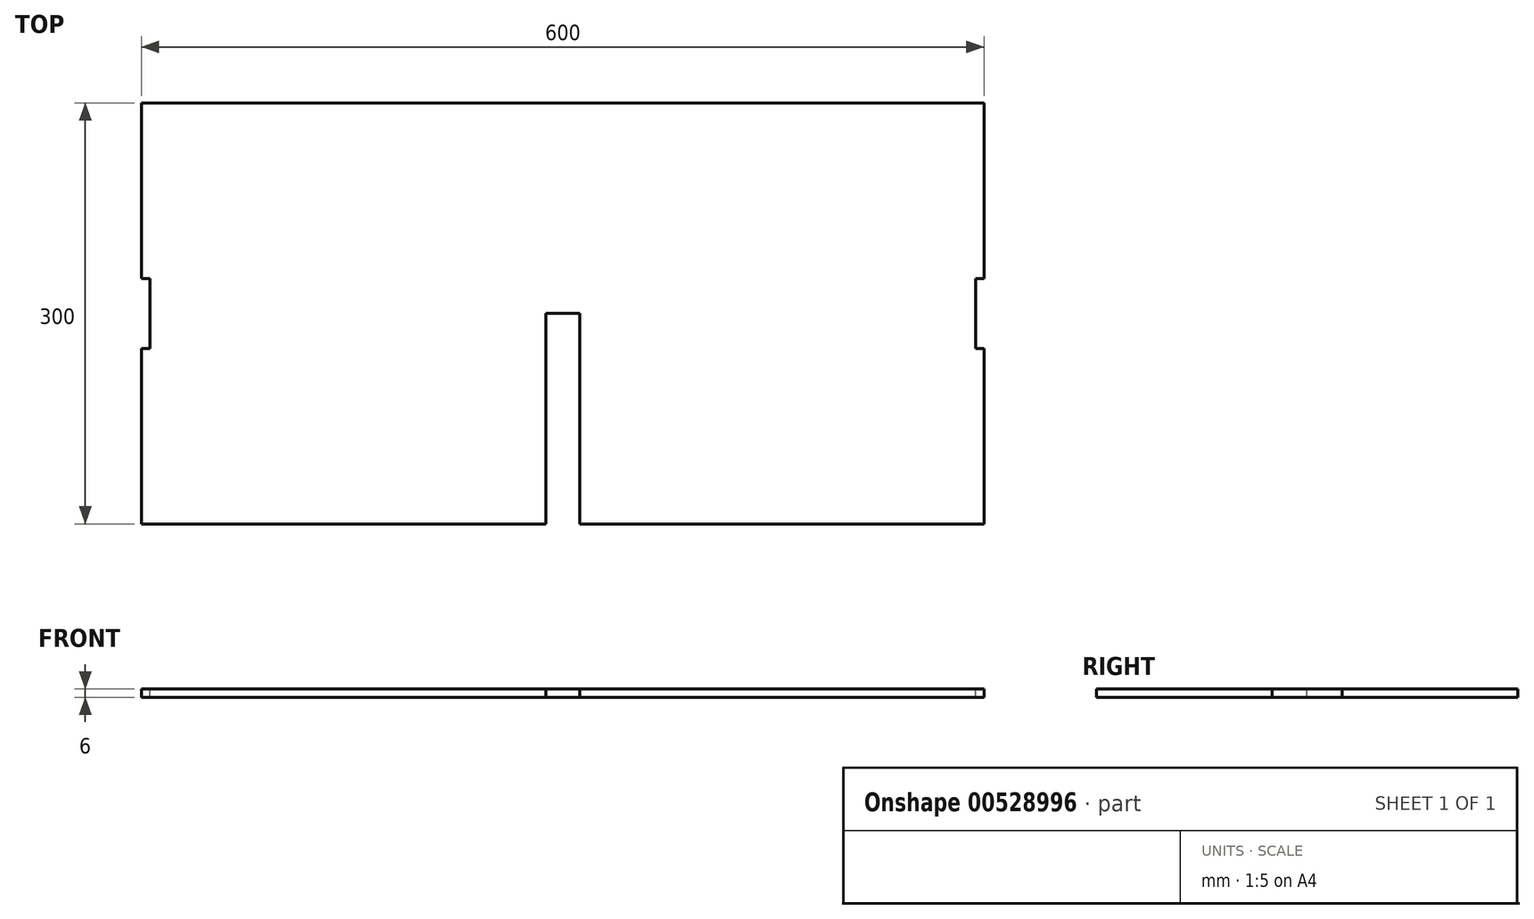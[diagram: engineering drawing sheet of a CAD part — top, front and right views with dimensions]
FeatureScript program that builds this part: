
annotation { "Feature Type Name" : "Feature", "Feature Type Description" : "" }
export const myFeature = defineFeature(function(context is Context, id is Id, definition is map)
    precondition{}
    {
        {
            var Q0;
            Q0=qCreatedBy(makeId("Front.planeOp"),FACE);
            var sketch = newSketch(context, id + "F0", { "sketchPlane" : qUnion([Q0])});
            skLineSegment(sketch, "E0.bottom", {"start": v(-213.98, 78.73) * mm, "end": v(386.02, 78.73) * mm});
            skLineSegment(sketch, "E0.top", {"start": v(-213.98, 72.73) * mm, "end": v(386.02, 72.73) * mm});
            skLineSegment(sketch, "E0.left", {"start": v(-213.98, 78.73) * mm, "end": v(-213.98, 72.73) * mm});
            skLineSegment(sketch, "E0.right", {"start": v(386.02, 78.73) * mm, "end": v(386.02, 72.73) * mm});
            skLineSegment(sketch, "E1", {"start": v(74.02, 78.73) * mm, "end": v(74.02, 72.73) * mm});
            skLineSegment(sketch, "E2", {"start": v(98.02, 78.73) * mm, "end": v(98.02, 72.73) * mm});
            skSolve(sketch);
        }
        {
            var Q0;
            Q0=qSketchRegion(id+"F0",true);
            extrude(context, id + "F1", {"entities" : qUnion([Q0]), "depth" : 300 * mm, "offsetDistance" : 25 * mm});
        }
        {
            var Q0;
            Q0=makeQuery(id+"F1.opExtrude","SWEPT_FACE",FACE,{"disambiguationData":[OSD([sQuery(id+"F0.wireOp",EDGE,"E0.bottom")])]});
            var sketch = newSketch(context, id + "F2", { "sketchPlane" : qUnion([Q0])});
            skLineSegment(sketch, "E3", {"start": v(-213.98, 0) * mm, "end": v(-213.98, -300) * mm});
            skLineSegment(sketch, "E4", {"start": v(386.02, 0) * mm, "end": v(386.02, -300) * mm});
            skLineSegment(sketch, "E5", {"start": v(98.02, -150) * mm, "end": v(98.02, -300) * mm});
            skLineSegment(sketch, "E6", {"start": v(74.02, -150) * mm, "end": v(74.02, -300) * mm});
            skLineSegment(sketch, "E7", {"start": v(98.02, -150) * mm, "end": v(74.02, -150) * mm});
            skLineSegment(sketch, "E8", {"start": v(-213.98, -175) * mm, "end": v(-207.98, -175) * mm});
            skLineSegment(sketch, "E9", {"start": v(-207.98, -175) * mm, "end": v(-207.98, -125) * mm});
            skLineSegment(sketch, "E10", {"start": v(-207.98, -125) * mm, "end": v(-213.98, -125) * mm});
            skLineSegment(sketch, "E11.MirrorCS", {"start": v(392.02, -175) * mm, "end": v(380.02, -175) * mm});
            skLineSegment(sketch, "E12.MirrorCS", {"start": v(380.02, -175) * mm, "end": v(380.02, -125) * mm});
            skLineSegment(sketch, "E13.MirrorCS", {"start": v(380.02, -125) * mm, "end": v(392.02, -125) * mm});
            skSolve(sketch);
        }
        {
            var Q0;
            {var subQ0=sQuery(id+"F2.wireOp",EDGE,"E8");Q0=makeQuery(id+"F2.imprint","IMPRINT",FACE,{"disambiguationData":[TD([[makeQuery(id+"F2.imprint","IMPRINT",EDGE,{"derivedFrom":subQ0}),1.0]])]});}
            var Q1;
            {var subQ0=sQuery(id+"F2.wireOp",EDGE,"E5");Q1=makeQuery(id+"F2.imprint","IMPRINT",FACE,{"disambiguationData":[TD([[makeQuery(id+"F2.imprint","IMPRINT",EDGE,{"derivedFrom":subQ0}),-1.0]])]});}
            var Q2;
            {var subQ0=sQuery(id+"F2.wireOp",EDGE,"E11.MirrorCS");Q2=makeQuery(id+"F2.imprint","IMPRINT",FACE,{"disambiguationData":[TD([[makeQuery(id+"F2.imprint","IMPRINT",EDGE,{"derivedFrom":subQ0}),-1.0]])]});}
            extrude(context, id + "F3", {"entities" : qUnion([Q0, Q1, Q2]), "operationType" : NewBodyOperationType.REMOVE, "oppositeDirection" : true, "depth" : 25 * mm});
        }
    });
